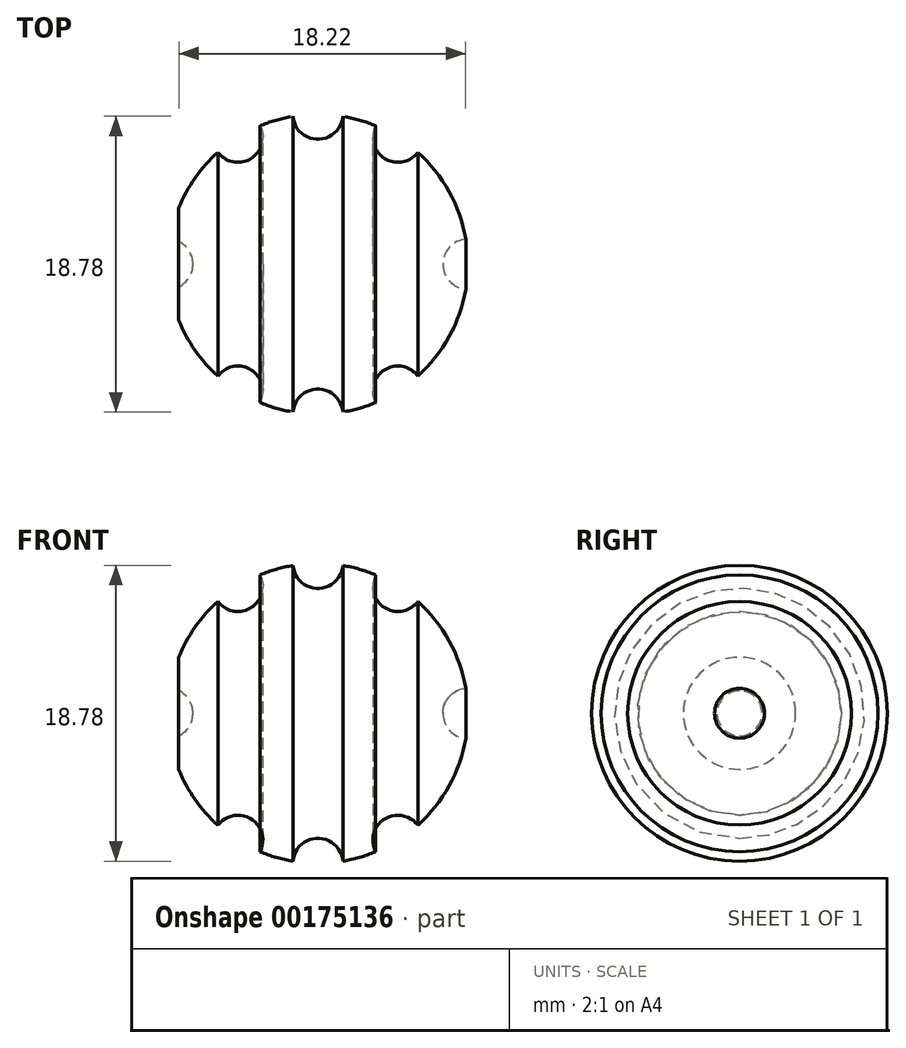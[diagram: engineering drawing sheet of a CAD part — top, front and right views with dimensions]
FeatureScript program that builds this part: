
annotation { "Feature Type Name" : "Feature", "Feature Type Description" : "" }
export const myFeature = defineFeature(function(context is Context, id is Id, definition is map)
    precondition{}
    {
        {
            var Q0;
            Q0=qCreatedBy(makeId("Top.planeOp"),FACE);
            var sketch = newSketch(context, id + "F0", { "sketchPlane" : qUnion([Q0])});
            skArc(sketch, "E0", {"start": v(0, -9.53) * mm, "mid": v(9.53, 0) * mm, "end": v(0, 9.53) * mm});
            skLineSegment(sketch, "E1", {"start": v(0, 9.53) * mm, "end": v(0, -9.53) * mm});
            skSolve(sketch);
        }
        {
            var Q0;
            Q0=makeQuery(id+"F0.imprint","IMPRINT",FACE,{"disambiguationData":[TD([[makeQuery(id+"F0.imprint","IMPRINT",EDGE,{"derivedFrom":sQuery(id+"F0.wireOp",EDGE,"E0")}),1.0]])]});
            var Q1;
            Q1=sQuery(id+"F0.wireOp",EDGE,"E1");
            revolve(context, id + "F1", {"entities" : qUnion([Q0]), "axis" : qUnion([Q1]), "revolveType" : RevolveType.FULL});
        }
        {
            var Q0;
            Q0=qCreatedBy(makeId("Front.planeOp"),FACE);
            var sketch = newSketch(context, id + "F2", { "sketchPlane" : qUnion([Q0])});
            skCircle(sketch, "E2", {"center": v(0, 0) * mm, "radius": 9.53 * mm, "construction": true});
            skCircle(sketch, "E3", {"center": v(0, 9.53) * mm, "radius": 1.59 * mm});
            skCircle(sketch, "E4", {"center": v(5.08, 8.06) * mm, "radius": 1.59 * mm});
            skCircle(sketch, "E5", {"center": v(-5.08, 8.06) * mm, "radius": 1.59 * mm});
            skLineSegment(sketch, "E6", {"start": v(-9.53, 0) * mm, "end": v(9.53, 0) * mm, "construction": true});
            skSolve(sketch);
        }
        {
            var Q0;
            Q0=makeQuery(id+"F2.imprint","IMPRINT",FACE,{"disambiguationData":[TD([[makeQuery(id+"F2.imprint","IMPRINT",EDGE,{"derivedFrom":sQuery(id+"F2.wireOp",EDGE,"E5")}),1.0]])]});
            var Q1;
            Q1=makeQuery(id+"F2.imprint","IMPRINT",FACE,{"disambiguationData":[TD([[makeQuery(id+"F2.imprint","IMPRINT",EDGE,{"derivedFrom":sQuery(id+"F2.wireOp",EDGE,"E3")}),1.0]])]});
            var Q2;
            Q2=makeQuery(id+"F2.imprint","IMPRINT",FACE,{"disambiguationData":[TD([[makeQuery(id+"F2.imprint","IMPRINT",EDGE,{"derivedFrom":sQuery(id+"F2.wireOp",EDGE,"E4")}),1.0]])]});
            var Q3;
            Q3=sQuery(id+"F2.wireOp",EDGE,"E6");
            revolve(context, id + "F3", {"operationType" : NewBodyOperationType.REMOVE, "entities" : qUnion([Q0, Q1, Q2]), "axis" : qUnion([Q3]), "revolveType" : RevolveType.FULL, "oppositeDirection" : true});
        }
        {
            var Q0;
            Q0=qCreatedBy(makeId("Front.planeOp"),FACE);
            var sketch = newSketch(context, id + "F4", { "sketchPlane" : qUnion([Q0])});
            skArc(sketch, "E7", {"start": v(-6.35, 7.1) * mm, "mid": v(-9.53, 0) * mm, "end": v(-6.35, -7.1) * mm, "construction": true});
            skArc(sketch, "E8", {"start": v(6.35, -7.1) * mm, "mid": v(9.53, 0) * mm, "end": v(6.35, 7.1) * mm, "construction": true});
            skCircle(sketch, "E9", {"center": v(-9.53, 0) * mm, "radius": 1.59 * mm});
            skCircle(sketch, "E10", {"center": v(9.53, 0) * mm, "radius": 1.59 * mm});
            skLineSegment(sketch, "E11", {"start": v(-11.11, 0) * mm, "end": v(11.11, 0) * mm});
            skLineSegment(sketch, "E12.0", {"start": v(-6.35, -7.1) * mm, "end": v(-6.35, 7.1) * mm, "construction": true});
            skLineSegment(sketch, "E13.0", {"start": v(6.35, 7.1) * mm, "end": v(6.35, -7.1) * mm, "construction": true});
            skSolve(sketch);
        }
        {
            var Q0;
            {var subQ0=sQuery(id+"F4.wireOp",EDGE,"E11");var subQ1=sQuery(id+"F4.wireOp",EDGE,"E9");var subQ2=makeQuery(id+"F4.imprint","INTERSECT",VERTEX,{"disambiguationData":[OD(0.0)],"derivedFrom":[subQ1,subQ0]});Q0=makeQuery(id+"F4.imprint","IMPRINT",FACE,{"disambiguationData":[TD([[makeQuery(id+"F4.imprint","IMPRINT",EDGE,{"disambiguationData":[TD([[subQ2,-1.0]])],"derivedFrom":subQ1}),1.0]])]});}
            var Q1;
            {var subQ0=sQuery(id+"F4.wireOp",EDGE,"E11");var subQ1=sQuery(id+"F4.wireOp",EDGE,"E10");var subQ2=makeQuery(id+"F4.imprint","INTERSECT",VERTEX,{"disambiguationData":[OD(0.0)],"derivedFrom":[subQ1,subQ0]});Q1=makeQuery(id+"F4.imprint","IMPRINT",FACE,{"disambiguationData":[TD([[makeQuery(id+"F4.imprint","IMPRINT",EDGE,{"disambiguationData":[TD([[subQ2,1.0]])],"derivedFrom":subQ1}),1.0]])]});}
            var Q2;
            Q2=sQuery(id+"F4.wireOp",EDGE,"E11");
            revolve(context, id + "F5", {"operationType" : NewBodyOperationType.REMOVE, "entities" : qUnion([Q0, Q1]), "axis" : qUnion([Q2]), "revolveType" : RevolveType.FULL, "oppositeDirection" : true});
        }
        {
            var Q0;
            Q0=qCreatedBy(makeId("Front.planeOp"),FACE);
            var sketch = newSketch(context, id + "F6", { "sketchPlane" : qUnion([Q0])});
            skLineSegment(sketch, "E14.bottom", {"start": v(-10.54, 5.8) * mm, "end": v(-8.83, 5.8) * mm});
            skLineSegment(sketch, "E14.top", {"start": v(-10.54, -6.16) * mm, "end": v(-8.83, -6.16) * mm});
            skLineSegment(sketch, "E14.left", {"start": v(-10.54, 5.8) * mm, "end": v(-10.54, -6.16) * mm});
            skLineSegment(sketch, "E14.right", {"start": v(-8.83, 5.8) * mm, "end": v(-8.83, -6.16) * mm});
            skSolve(sketch);
        }
        {
            var Q0;
            Q0=makeQuery(id+"F6.imprint","IMPRINT",FACE,{"disambiguationData":[TD([[makeQuery(id+"F6.imprint","IMPRINT",EDGE,{"derivedFrom":sQuery(id+"F6.wireOp",EDGE,"E14.bottom")}),-1.0]])]});
            extrude(context, id + "F7", {"entities" : qUnion([Q0]), "operationType" : NewBodyOperationType.REMOVE, "endBound" : BoundingType.THROUGH_ALL, "oppositeDirection" : true, "depth" : 25.4 * mm, "hasSecondDirection" : true, "secondDirectionBound" : SecondDirectionBoundingType.THROUGH_ALL, "secondDirectionOppositeDirection" : false, "secondDirectionDepth" : 25.4 * mm});
        }
    });
